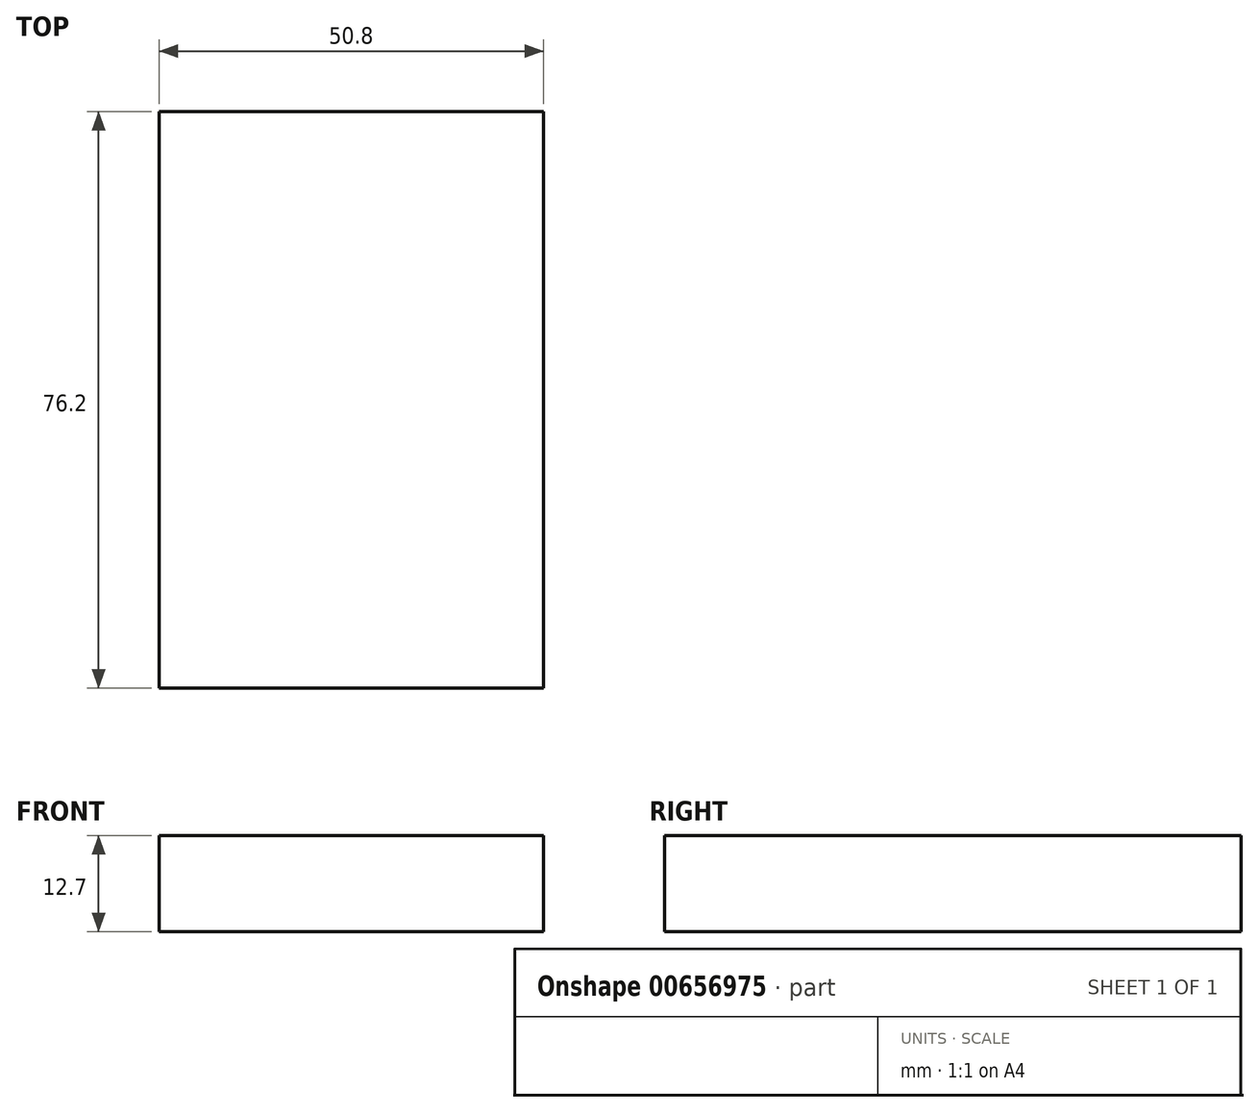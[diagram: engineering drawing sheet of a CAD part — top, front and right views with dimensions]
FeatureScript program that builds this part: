
annotation { "Feature Type Name" : "Feature", "Feature Type Description" : "" }
export const myFeature = defineFeature(function(context is Context, id is Id, definition is map)
    precondition{}
    {
        {
            var Q0;
            Q0=qCreatedBy(makeId("Front.planeOp"),FACE);
            var sketch = newSketch(context, id + "F0", { "sketchPlane" : qUnion([Q0])});
            skLineSegment(sketch, "E0", {"start": v(-62.13, -39.83) * mm, "end": v(-11.33, -39.83) * mm});
            skLineSegment(sketch, "E1", {"start": v(-11.33, -39.83) * mm, "end": v(-11.33, -27.13) * mm});
            skLineSegment(sketch, "E2", {"start": v(-11.33, -27.13) * mm, "end": v(-62.13, -27.13) * mm});
            skLineSegment(sketch, "E3", {"start": v(-62.13, -27.13) * mm, "end": v(-62.13, -39.83) * mm});
            skSolve(sketch);
        }
        {
            var Q0;
            Q0=makeQuery(id+"F0.imprint","IMPRINT",FACE,{"disambiguationData":[TD([[makeQuery(id+"F0.imprint","IMPRINT",EDGE,{"derivedFrom":sQuery(id+"F0.wireOp",EDGE,"E0")}),1.0]])]});
            extrude(context, id + "F1", {"entities" : qUnion([Q0]), "depth" : 76.2 * mm, "offsetDistance" : 25.4 * mm});
        }
    });
